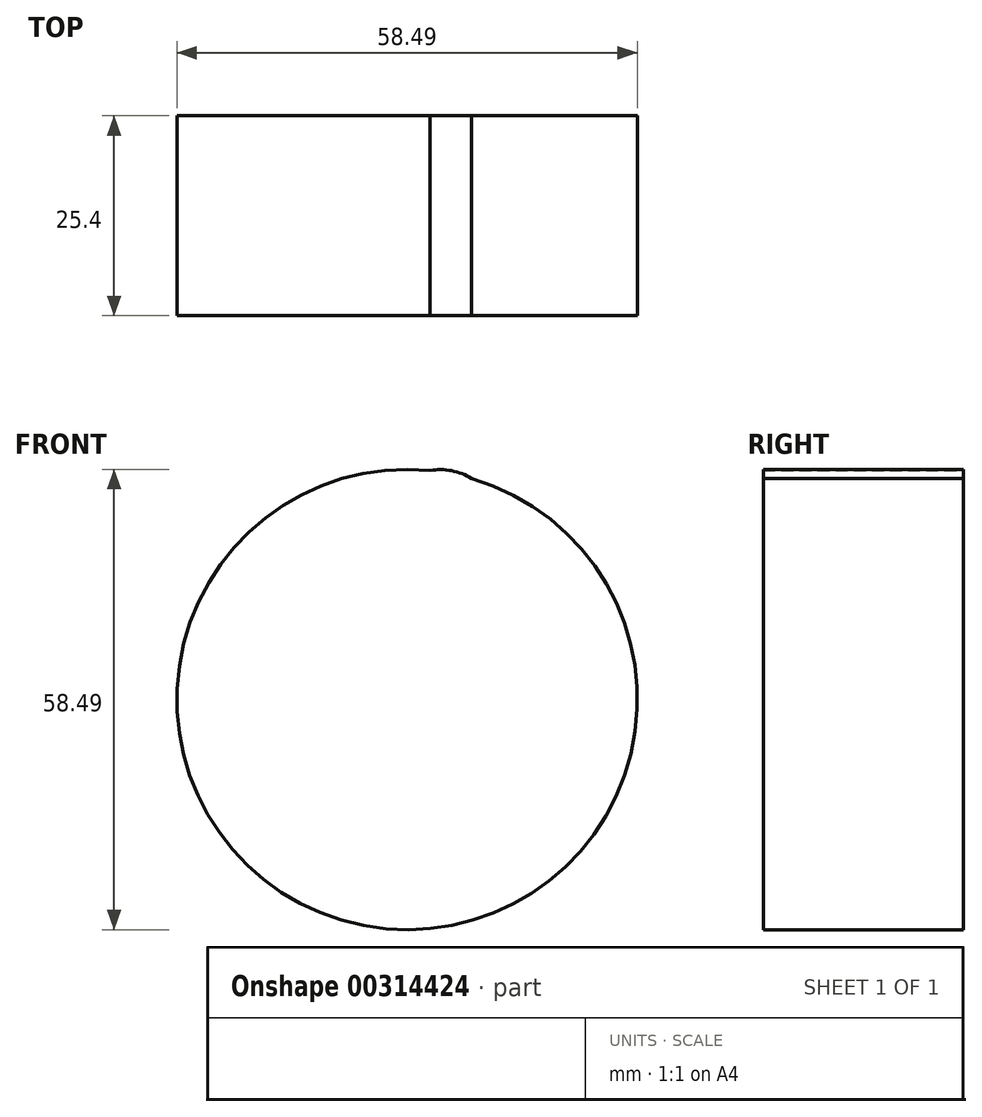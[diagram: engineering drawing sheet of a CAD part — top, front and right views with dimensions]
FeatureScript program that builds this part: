
annotation { "Feature Type Name" : "Feature", "Feature Type Description" : "" }
export const myFeature = defineFeature(function(context is Context, id is Id, definition is map)
    precondition{}
    {
        {
            var Q0;
            Q0=qCreatedBy(makeId("Front.planeOp"),FACE);
            var sketch = newSketch(context, id + "F0", { "sketchPlane" : qUnion([Q0])});
            skCircle(sketch, "E0", {"center": v(0, -4.7) * mm, "radius": 7.7 * mm});
            skCircle(sketch, "E1", {"center": v(-4.17, -26.2) * mm, "radius": 29.24 * mm});
            skSolve(sketch);
        }
        {
            var Q0;
            Q0 = qSketchRegion(id + "F0", true);
            extrude(context, id + "F1", {"entities" : qUnion([Q0]), "depth" : 25.4 * mm});
        }
    });
